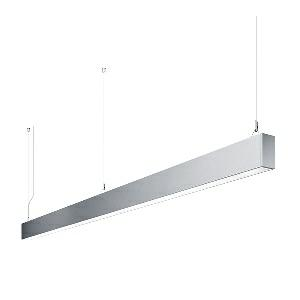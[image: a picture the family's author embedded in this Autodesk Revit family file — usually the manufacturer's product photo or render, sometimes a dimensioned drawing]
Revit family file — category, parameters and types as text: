
# Revit family: idoo_line_-_ilp_6000_vtl_d_00806472_b4ad
name_source: partatom
category: Lighting Fixtures
units: mm (PartAtom-declared; Revit-internal decimal feet)

## family parameters
Cut with Voids When Loaded = No
Host = Face
Light Source = No
Part Type = Normal
Room Calculation Point = No
Round Connector Dimension = Use Diameter
Shared = No

## types (1)
- IDOO.line - ILP 6000/VTL/D (1 x LED, 6150 lm, 2700-6500K)
    Apparent Load = 63 VA
    Approval mark = CE
    CIE Flux Codes = 66 91 98 40 100
    Color Rendering = 90-100
    Color Temperature = 2700-6500K
    Control Gear = Electronic ballast
    Default Elevation = 1800 mm
    Description = ILP 6000/VTL/D|Suspended luminaire|light source: LED|connected load: 220-240 V, 50/60 Hz|Power consumption: approx. 63 W|standby: approx. 0,25|luminous flux: 6150 lm|luminous efficacy: 97 lm/W|light distribution: Direct/indirect|direct ratio: approx. 40 %|colour temperature: Cold white, ca. 2700-6500 K|color rendering index (CRI): >= 90|chromaticity tolerance:  3 SDCM|System of protection: IP 40|technology: Continuously dimmable|luminaire body|material: Sectional aluminium|colour: Silver|lamp cover: Acrylic (PMMA), Clear|mains lead: 2.00 m With free stranded wires|Fastening: Steel cable 0.3 - 0.7 m|glare control: Prism aperture|luminance(L65): <= 2700 cd/m|unified glare rating(4H 8H): <=  16|special features: Specified values at approx. 4000 K, DALI Load 1x, External control required for Dali Device type 8, Flicker-free, Constant luminous flux between 2700 and 6500 K, Constant colour temperature over the whole dimming range, Suitable as emergency lighting|
    Frequency = 50 Hz
    Height = 110 mm
    Lamp = 1 x LED
    Lamp Light Flux = 6150 lm
    Lamp count = 1
    Length = 2256 mm
    Luminous efficacy = 98 lm/W
    Manufacturer = Waldmann
    ModVariant = No
    Model = 00806472
    Mounting Place = Ceiling
    Mounting Type = Pendant
    Number of Poles = 1
    OnlyDefault = Yes
    Power Factor = 1
    Product Name = IDOO.line - ILP 6000/VTL/D
    Product group = Suspended luminaire
    ProductGroupID = 9
    Protection Class = Protection class I
    Protection Degree = IP 40
    RLX_Detail_Level = 1
    RLX_Emergency_Light_Flux = 0 lm
    RLX_Emergency_Type = 0
    RLX_Emergency_Type_DB = No
    RlxData = <blob elided: 23561 chars, md5=312c53ee>
    Socket = socket
    Standby Power = 0 W
    System Light Flux = 6150 lm
    System Power = 63 W
    Type Comments = Product without accessories
    Type Image = 113294000-00692533.jpg
    URL = http://relux.com
    VarID = ---
    Voltage = 230 V
    Voltage Range = 220-240 V
    Weight = 0.00 kg
    Width = 60 mm  [stored 0.19685 ft]

note: [stored X ft] marks values corroborated as IEEE doubles in the binary element streams (Revit-internal decimal feet)

## geometry (parser evidence)
native form markers: Blend x4, Sweep x13
no freeform markers — native parametric forms only
